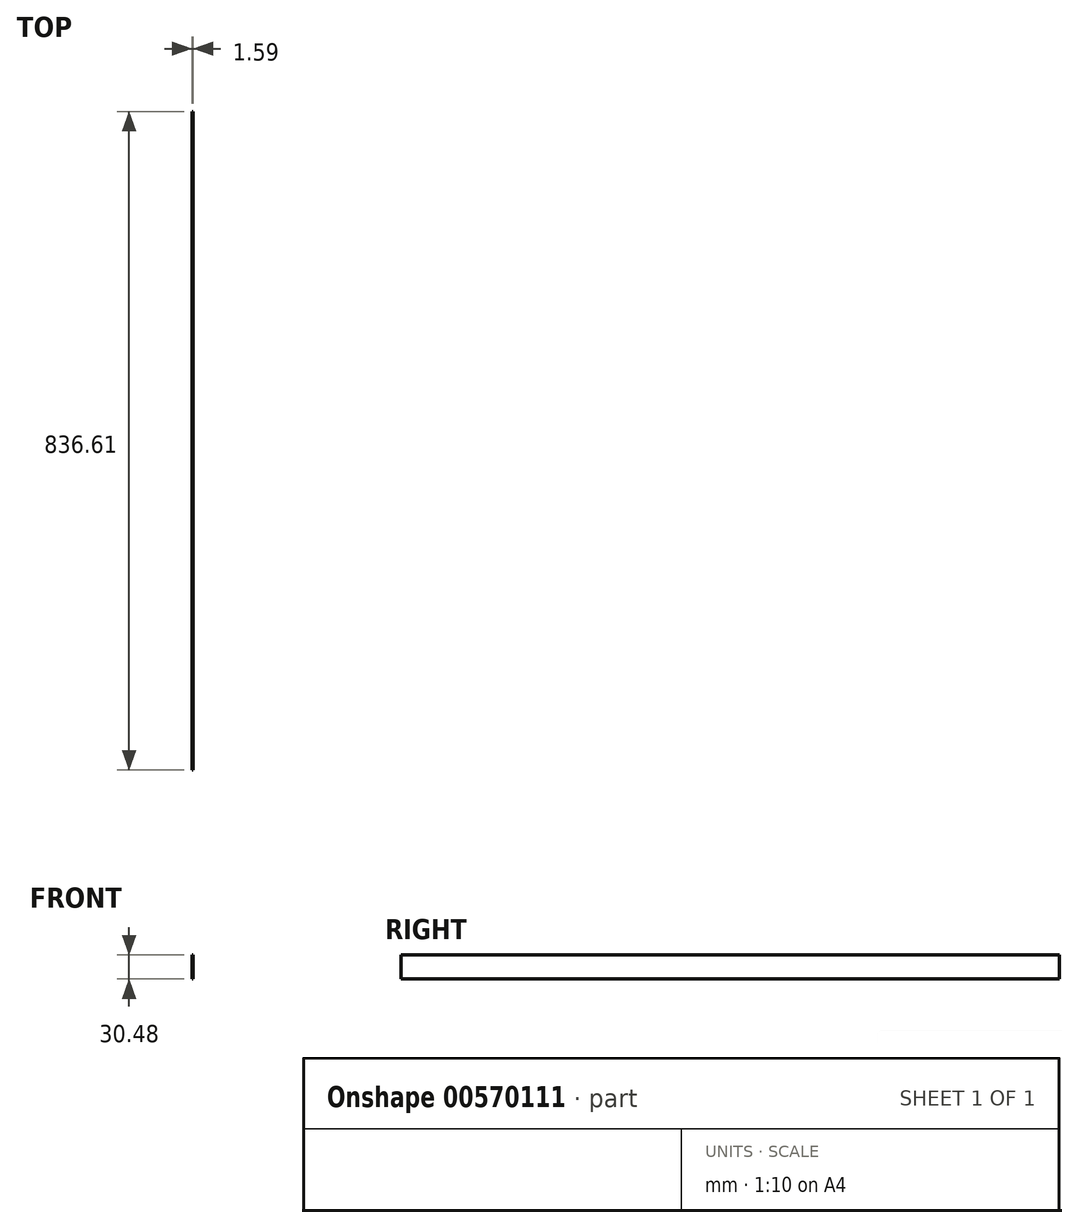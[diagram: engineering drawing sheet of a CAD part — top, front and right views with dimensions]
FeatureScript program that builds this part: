
annotation { "Feature Type Name" : "Feature", "Feature Type Description" : "" }
export const myFeature = defineFeature(function(context is Context, id is Id, definition is map)
    precondition{}
    {
        {
            var Q0;
            Q0=qCreatedBy(makeId("Front.planeOp"),FACE);
            var sketch = newSketch(context, id + "F0", { "sketchPlane" : qUnion([Q0])});
            skLineSegment(sketch, "E0.bottom", {"start": v(0, 0) * mm, "end": v(1.59, 0) * mm});
            skLineSegment(sketch, "E0.top", {"start": v(0, -30.48) * mm, "end": v(1.59, -30.48) * mm});
            skLineSegment(sketch, "E0.left", {"start": v(0, 0) * mm, "end": v(0, -30.48) * mm});
            skLineSegment(sketch, "E0.right", {"start": v(1.59, 0) * mm, "end": v(1.59, -30.48) * mm});
            skSolve(sketch);
        }
        {
            var Q0;
            Q0=makeQuery(id+"F0.imprint","IMPRINT",FACE,{"disambiguationData":[TD([[makeQuery(id+"F0.imprint","IMPRINT",EDGE,{"derivedFrom":sQuery(id+"F0.wireOp",EDGE,"E0.bottom")}),-1.0]])]});
            extrude(context, id + "F1", {"entities" : qUnion([Q0]), "depth" : 836.6 * mm, "offsetDistance" : 25.4 * mm});
        }
    });
